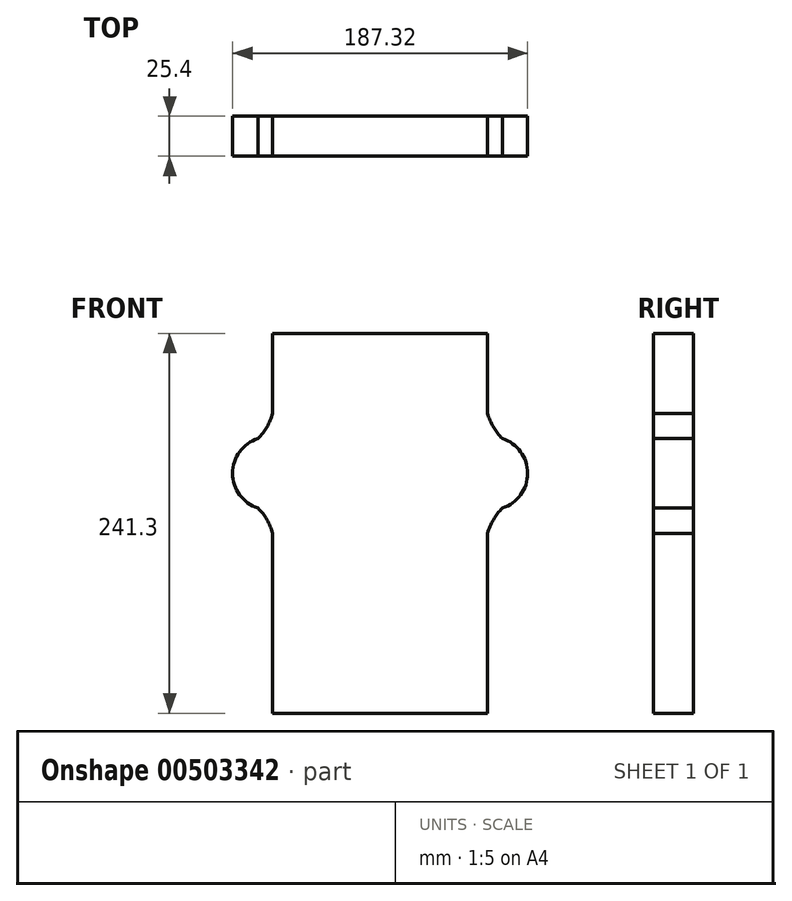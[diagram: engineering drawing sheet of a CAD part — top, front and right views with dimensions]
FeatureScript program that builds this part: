
annotation { "Feature Type Name" : "Feature", "Feature Type Description" : "" }
export const myFeature = defineFeature(function(context is Context, id is Id, definition is map)
    precondition{}
    {
        {
            var Q0;
            Q0=qCreatedBy(makeId("Front.planeOp"),FACE);
            var sketch = newSketch(context, id + "F0", { "sketchPlane" : qUnion([Q0])});
            skLineSegment(sketch, "E0.bottom", {"start": v(68.26, 120.65) * mm, "end": v(-68.26, 120.65) * mm});
            skLineSegment(sketch, "E0.top", {"start": v(68.26, -120.65) * mm, "end": v(-68.26, -120.65) * mm});
            skLineSegment(sketch, "E0.left", {"start": v(68.26, 120.65) * mm, "end": v(68.26, -120.65) * mm});
            skLineSegment(sketch, "E0.right", {"start": v(-68.26, 120.65) * mm, "end": v(-68.26, -120.65) * mm});
            skPoint(sketch, "E0.middle", {"position": v(0, 0) * mm});
            skSolve(sketch);
        }
        {
            var Q0;
            Q0=makeQuery(id+"F0.imprint","IMPRINT",FACE,{"disambiguationData":[TD([[makeQuery(id+"F0.imprint","IMPRINT",EDGE,{"derivedFrom":sQuery(id+"F0.wireOp",EDGE,"E0.bottom")}),1.0]])]});
            extrude(context, id + "F1", {"entities" : qUnion([Q0]), "depth" : 25.4 * mm});
        }
        {
            var Q0;
            Q0=makeQuery(id+"F1.opExtrude","CAP_FACE",FACE,{"disambiguationData":[OSD([sQuery(id+"F0.wireOp",EDGE,"E0.bottom"),sQuery(id+"F0.wireOp",EDGE,"E0.top"),sQuery(id+"F0.wireOp",EDGE,"E0.left"),sQuery(id+"F0.wireOp",EDGE,"E0.right")])],"isStart":false});
            var sketch = newSketch(context, id + "F2", { "sketchPlane" : qUnion([Q0])});
            skPoint(sketch, "E1", {"position": v(68.26, 69.85) * mm});
            skPoint(sketch, "E2", {"position": v(68.26, -6.35) * mm});
            skPoint(sketch, "E3", {"position": v(93.66, 44.45) * mm});
            skPoint(sketch, "E4", {"position": v(93.66, 19.05) * mm});
            skArc(sketch, "E5", {"start": v(68.26, 69.85) * mm, "mid": v(77.63, 53.81) * mm, "end": v(93.66, 44.45) * mm});
            skArc(sketch, "E6", {"start": v(93.66, 19.05) * mm, "mid": v(77.63, 9.69) * mm, "end": v(68.26, -6.35) * mm});
            skPoint(sketch, "E7.startSnap0", {"position": v(77.63, 53.81) * mm});
            skLineSegment(sketch, "E8", {"start": v(93.66, 44.45) * mm, "end": v(93.66, 19.05) * mm});
            skArc(sketch, "E9", {"start": v(77.63, 9.69) * mm, "mid": v(93.66, 31.75) * mm, "end": v(77.63, 53.81) * mm});
            skSolve(sketch);
        }
        {
            var Q0;
            {var subQ0=sQuery(id+"F2.wireOp",EDGE,"E9");var subQ1=sQuery(id+"F2.wireOp",EDGE,"E5");var subQ2=makeQuery(id+"F2.imprint","INTERSECT",VERTEX,{"disambiguationData":[OD(0.0)],"derivedFrom":[subQ1,subQ0]});Q0=makeQuery(id+"F2.imprint","IMPRINT",FACE,{"disambiguationData":[TD([[makeQuery(id+"F2.imprint","IMPRINT",EDGE,{"disambiguationData":[TD([[subQ2,-1.0]])],"derivedFrom":subQ1}),1.0]])]});}
            var Q1;
            {var subQ0=sQuery(id+"F2.wireOp",EDGE,"E9");var subQ1=sQuery(id+"F2.wireOp",EDGE,"E6");var subQ2=makeQuery(id+"F2.imprint","INTERSECT",VERTEX,{"disambiguationData":[OD(0.0)],"derivedFrom":[subQ1,subQ0]});Q1=makeQuery(id+"F2.imprint","IMPRINT",FACE,{"disambiguationData":[TD([[makeQuery(id+"F2.imprint","IMPRINT",EDGE,{"disambiguationData":[TD([[subQ2,1.0]])],"derivedFrom":subQ1}),1.0]])]});}
            var Q2;
            {var subQ4=sQuery(id+"F2.wireOp",EDGE,"E5");var subQ7=makeQuery(id+"F1.opExtrude","CAP_EDGE",EDGE,{"disambiguationData":[OSD([sQuery(id+"F0.wireOp",EDGE,"E0.left")])],"isStart":false});var subQ9=makeQuery(id+"F2.imprint","INTERSECT",VERTEX,{"derivedFrom":[subQ7,subQ4]});Q2=makeQuery(id+"F2.imprint","IMPRINT",FACE,{"disambiguationData":[TD([[makeQuery(id+"F2.imprint","IMPRINT",EDGE,{"disambiguationData":[TD([[subQ9,-1.0]])],"derivedFrom":subQ4}),-1.0]])]});}
            extrude(context, id + "F3", {"entities" : qUnion([Q0, Q1, Q2]), "oppositeDirection" : true, "depth" : 25.4 * mm});
        }
        {
            var Q0;
            Q0=makeQuery(id+"F3.opExtrude","SWEPT_BODY",BODY,{"disambiguationData":[OSD([sQuery(id+"F0.wireOp",EDGE,"E0.left"),sQuery(id+"F2.wireOp",EDGE,"E5"),sQuery(id+"F2.wireOp",EDGE,"E6"),sQuery(id+"F2.wireOp",EDGE,"E9")])]});
            var Q1;
            Q1=qCreatedBy(makeId("Right.planeOp"),FACE);
            mirror(context, id + "F4", {"operationType" : NewBodyOperationType.ADD, "entities" : qUnion([Q0]), "mirrorPlane" : qUnion([Q1])});
        }
    });
